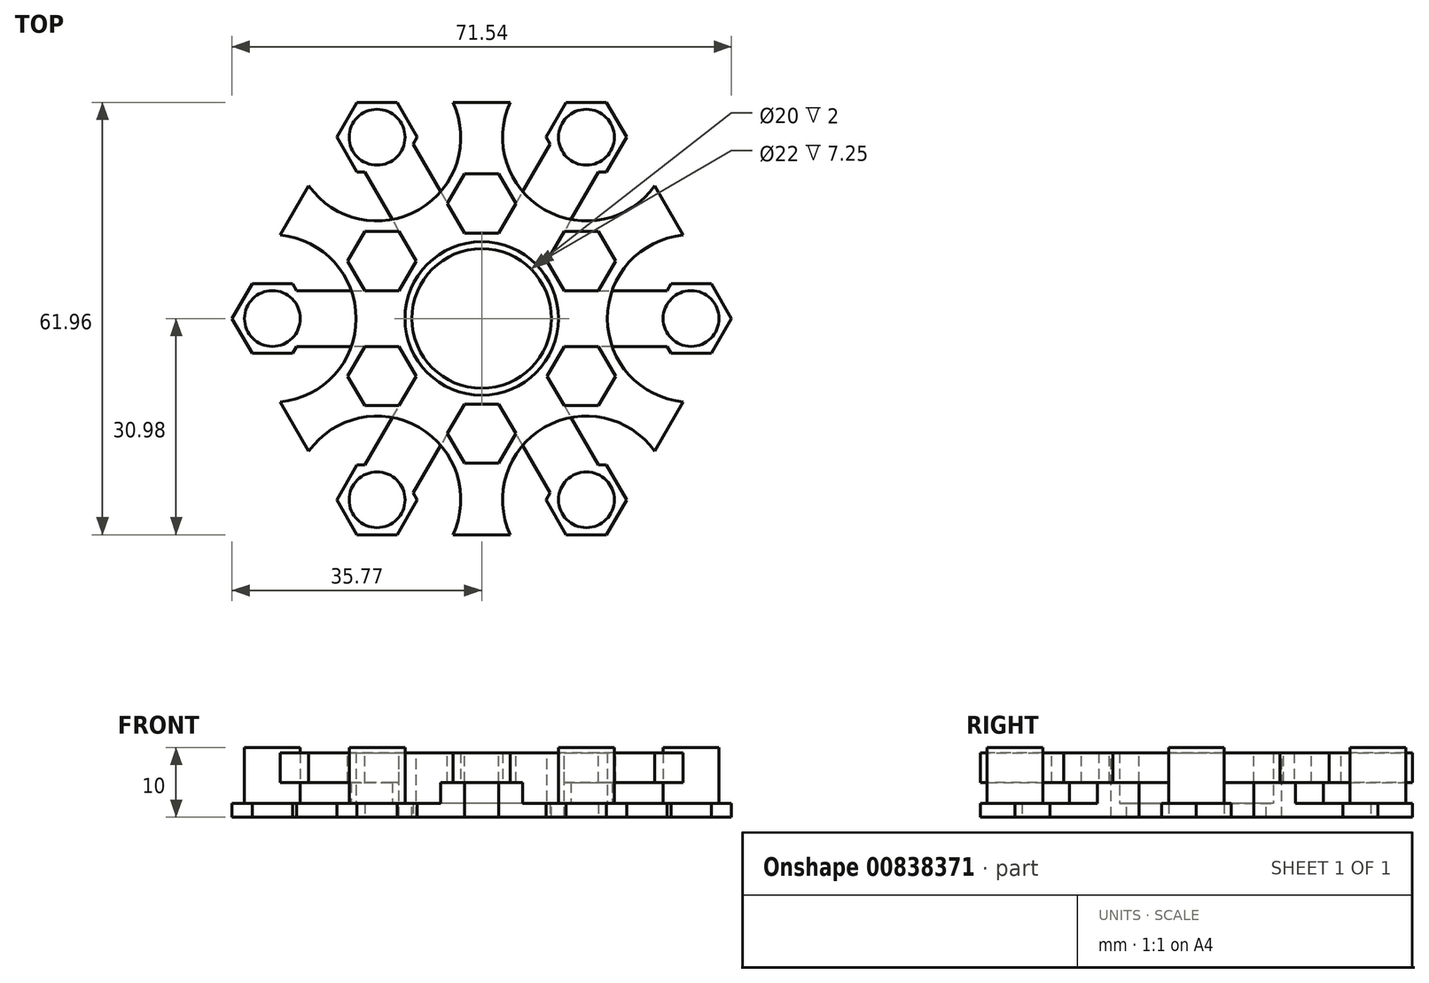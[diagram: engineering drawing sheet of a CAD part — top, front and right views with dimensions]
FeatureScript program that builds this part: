
annotation { "Feature Type Name" : "Feature", "Feature Type Description" : "" }
export const myFeature = defineFeature(function(context is Context, id is Id, definition is map)
    precondition{}
    {
        {
            var Q0;
            Q0=qCreatedBy(makeId("Top.planeOp"),FACE);
            var sketch = newSketch(context, id + "F0", { "sketchPlane" : qUnion([Q0])});
            skCircle(sketch, "E0", {"center": v(0, 0) * mm, "radius": 11 * mm});
            skCircle(sketch, "E1.cCircle", {"center": v(0, 0) * mm, "radius": 25.98 * mm, "construction": true});
            skLineSegment(sketch, "E1.0", {"start": v(-15, 25.98) * mm, "end": v(15, 25.98) * mm});
            skLineSegment(sketch, "E1.1", {"start": v(15, 25.98) * mm, "end": v(30, 0) * mm});
            skLineSegment(sketch, "E1.2", {"start": v(30, 0) * mm, "end": v(15, -25.98) * mm});
            skLineSegment(sketch, "E1.3", {"start": v(15, -25.98) * mm, "end": v(-15, -25.98) * mm});
            skLineSegment(sketch, "E1.4", {"start": v(-15, -25.98) * mm, "end": v(-30, 0) * mm});
            skLineSegment(sketch, "E1.5", {"start": v(-30, 0) * mm, "end": v(-15, 25.98) * mm});
            skPoint(sketch, "E1.0.midPoint", {"position": v(0, 25.98) * mm});
            skCircle(sketch, "E2", {"center": v(-15, 25.98) * mm, "radius": 11 * mm});
            skCircle(sketch, "E3", {"center": v(15, 25.98) * mm, "radius": 11 * mm});
            skCircle(sketch, "E4", {"center": v(30, 0) * mm, "radius": 11 * mm});
            skCircle(sketch, "E5", {"center": v(15, -25.98) * mm, "radius": 11 * mm});
            skCircle(sketch, "E6", {"center": v(-15, -25.98) * mm, "radius": 11 * mm});
            skCircle(sketch, "E7", {"center": v(-30, 0) * mm, "radius": 11 * mm});
            skCircle(sketch, "E8.cCircle", {"center": v(0, 0) * mm, "radius": 30.98 * mm, "construction": true});
            skLineSegment(sketch, "E8.0", {"start": v(-17.89, 30.98) * mm, "end": v(17.89, 30.98) * mm});
            skLineSegment(sketch, "E8.1", {"start": v(17.89, 30.98) * mm, "end": v(35.77, 0) * mm});
            skLineSegment(sketch, "E8.2", {"start": v(35.77, 0) * mm, "end": v(17.89, -30.98) * mm});
            skLineSegment(sketch, "E8.3", {"start": v(17.89, -30.98) * mm, "end": v(-17.89, -30.98) * mm});
            skLineSegment(sketch, "E8.4", {"start": v(-17.89, -30.98) * mm, "end": v(-35.77, 0) * mm});
            skLineSegment(sketch, "E8.5", {"start": v(-35.77, 0) * mm, "end": v(-17.89, 30.98) * mm});
            skPoint(sketch, "E8.0.midPoint", {"position": v(0, 30.98) * mm});
            skCircle(sketch, "E9", {"center": v(0, 0) * mm, "radius": 10 * mm});
            skCircle(sketch, "E10", {"center": v(-15, 25.98) * mm, "radius": 4 * mm});
            skCircle(sketch, "E11", {"center": v(-30, 0) * mm, "radius": 4 * mm});
            skCircle(sketch, "E12", {"center": v(-15, -25.98) * mm, "radius": 4 * mm});
            skCircle(sketch, "E13", {"center": v(15, -25.98) * mm, "radius": 4 * mm});
            skCircle(sketch, "E14", {"center": v(30, 0) * mm, "radius": 4 * mm});
            skCircle(sketch, "E15", {"center": v(15, 25.98) * mm, "radius": 4 * mm});
            skCircle(sketch, "E16", {"center": v(-30, 0) * mm, "radius": 12 * mm});
            skCircle(sketch, "E17", {"center": v(-15, 25.98) * mm, "radius": 12 * mm});
            skCircle(sketch, "E18", {"center": v(15, 25.98) * mm, "radius": 12 * mm});
            skCircle(sketch, "E19", {"center": v(30, 0) * mm, "radius": 12 * mm});
            skCircle(sketch, "E20", {"center": v(15, -25.98) * mm, "radius": 12 * mm});
            skCircle(sketch, "E21", {"center": v(-15, -25.98) * mm, "radius": 12 * mm});
            skSolve(sketch);
        }
        {
            var Q0;
            {var subQ0=sQuery(id+"F0.wireOp",EDGE,"E6");var subQ1=sQuery(id+"F0.wireOp",EDGE,"E1.4");var subQ2=makeQuery(id+"F0.imprint","INTERSECT",VERTEX,{"derivedFrom":[subQ1,subQ0]});Q0=makeQuery(id+"F0.imprint","IMPRINT",FACE,{"disambiguationData":[TD([[makeQuery(id+"F0.imprint","IMPRINT",EDGE,{"disambiguationData":[TD([[subQ2,-1.0]])],"derivedFrom":subQ1}),1.0]])]});}
            var Q1;
            {var subQ1=sQuery(id+"F0.wireOp",EDGE,"E6");var subQ3=sQuery(id+"F0.wireOp",EDGE,"E1.3");var subQ4=makeQuery(id+"F0.imprint","INTERSECT",VERTEX,{"derivedFrom":[subQ3,subQ1]});Q1=makeQuery(id+"F0.imprint","IMPRINT",FACE,{"disambiguationData":[TD([[makeQuery(id+"F0.imprint","IMPRINT",EDGE,{"disambiguationData":[TD([[subQ4,-1.0]])],"derivedFrom":subQ3}),1.0]])]});}
            var Q2;
            {var subQ0=sQuery(id+"F0.wireOp",EDGE,"E1.4");var subQ1=sQuery(id+"F0.wireOp",EDGE,"E1.3");var subQ2=makeQuery(id+"F0.imprint","INTERSECT",VERTEX,{"derivedFrom":[subQ1,subQ0]});Q2=makeQuery(id+"F0.imprint","IMPRINT",FACE,{"disambiguationData":[TD([[makeQuery(id+"F0.imprint","IMPRINT",EDGE,{"disambiguationData":[TD([[subQ2,1.0]])],"derivedFrom":subQ1}),1.0]])]});}
            var Q3;
            {var subQ0=sQuery(id+"F0.wireOp",EDGE,"E1.4");var subQ1=sQuery(id+"F0.wireOp",EDGE,"E1.3");var subQ2=makeQuery(id+"F0.imprint","INTERSECT",VERTEX,{"derivedFrom":[subQ1,subQ0]});Q3=makeQuery(id+"F0.imprint","IMPRINT",FACE,{"disambiguationData":[TD([[makeQuery(id+"F0.imprint","IMPRINT",EDGE,{"disambiguationData":[TD([[subQ2,1.0]])],"derivedFrom":subQ1}),-1.0]])]});}
            var Q4;
            {var subQ0=sQuery(id+"F0.wireOp",EDGE,"E6");var subQ1=sQuery(id+"F0.wireOp",EDGE,"E1.3");var subQ2=makeQuery(id+"F0.imprint","INTERSECT",VERTEX,{"derivedFrom":[subQ1,subQ0]});Q4=makeQuery(id+"F0.imprint","IMPRINT",FACE,{"disambiguationData":[TD([[makeQuery(id+"F0.imprint","IMPRINT",EDGE,{"disambiguationData":[TD([[subQ2,-1.0]])],"derivedFrom":subQ1}),-1.0]])]});}
            var Q5;
            {var subQ1=sQuery(id+"F0.wireOp",EDGE,"E7");var subQ3=sQuery(id+"F0.wireOp",EDGE,"E1.4");var subQ4=makeQuery(id+"F0.imprint","INTERSECT",VERTEX,{"derivedFrom":[subQ3,subQ1]});Q5=makeQuery(id+"F0.imprint","IMPRINT",FACE,{"disambiguationData":[TD([[makeQuery(id+"F0.imprint","IMPRINT",EDGE,{"disambiguationData":[TD([[subQ4,-1.0]])],"derivedFrom":subQ3}),1.0]])]});}
            var Q6;
            {var subQ0=sQuery(id+"F0.wireOp",EDGE,"E1.5");var subQ1=sQuery(id+"F0.wireOp",EDGE,"E1.4");var subQ2=makeQuery(id+"F0.imprint","INTERSECT",VERTEX,{"derivedFrom":[subQ1,subQ0]});Q6=makeQuery(id+"F0.imprint","IMPRINT",FACE,{"disambiguationData":[TD([[makeQuery(id+"F0.imprint","IMPRINT",EDGE,{"disambiguationData":[TD([[subQ2,1.0]])],"derivedFrom":subQ1}),-1.0]])]});}
            var Q7;
            {var subQ0=sQuery(id+"F0.wireOp",EDGE,"E1.5");var subQ1=sQuery(id+"F0.wireOp",EDGE,"E1.4");var subQ2=makeQuery(id+"F0.imprint","INTERSECT",VERTEX,{"derivedFrom":[subQ1,subQ0]});Q7=makeQuery(id+"F0.imprint","IMPRINT",FACE,{"disambiguationData":[TD([[makeQuery(id+"F0.imprint","IMPRINT",EDGE,{"disambiguationData":[TD([[subQ2,1.0]])],"derivedFrom":subQ1}),1.0]])]});}
            var Q8;
            {var subQ0=sQuery(id+"F0.wireOp",EDGE,"E7");var subQ1=sQuery(id+"F0.wireOp",EDGE,"E1.4");var subQ2=makeQuery(id+"F0.imprint","INTERSECT",VERTEX,{"derivedFrom":[subQ1,subQ0]});Q8=makeQuery(id+"F0.imprint","IMPRINT",FACE,{"disambiguationData":[TD([[makeQuery(id+"F0.imprint","IMPRINT",EDGE,{"disambiguationData":[TD([[subQ2,-1.0]])],"derivedFrom":subQ1}),-1.0]])]});}
            var Q9;
            Q9=makeQuery(id+"F0.imprint","IMPRINT",FACE,{"disambiguationData":[TD([[makeQuery(id+"F0.imprint","IMPRINT",EDGE,{"derivedFrom":sQuery(id+"F0.wireOp",EDGE,"E0")}),-1.0]])]});
            var Q10;
            Q10=makeQuery(id+"F0.imprint","IMPRINT",FACE,{"disambiguationData":[TD([[makeQuery(id+"F0.imprint","IMPRINT",EDGE,{"derivedFrom":sQuery(id+"F0.wireOp",EDGE,"E0")}),1.0]])]});
            var Q11;
            {var subQ0=sQuery(id+"F0.wireOp",EDGE,"E5");var subQ1=sQuery(id+"F0.wireOp",EDGE,"E1.3");var subQ2=makeQuery(id+"F0.imprint","INTERSECT",VERTEX,{"derivedFrom":[subQ1,subQ0]});Q11=makeQuery(id+"F0.imprint","IMPRINT",FACE,{"disambiguationData":[TD([[makeQuery(id+"F0.imprint","IMPRINT",EDGE,{"disambiguationData":[TD([[subQ2,-1.0]])],"derivedFrom":subQ1}),1.0]])]});}
            var Q12;
            {var subQ1=sQuery(id+"F0.wireOp",EDGE,"E5");var subQ7=sQuery(id+"F0.wireOp",EDGE,"E1.2");var subQ8=makeQuery(id+"F0.imprint","INTERSECT",VERTEX,{"derivedFrom":[subQ7,subQ1]});Q12=makeQuery(id+"F0.imprint","IMPRINT",FACE,{"disambiguationData":[TD([[makeQuery(id+"F0.imprint","IMPRINT",EDGE,{"disambiguationData":[TD([[subQ8,-1.0]])],"derivedFrom":subQ7}),1.0]])]});}
            var Q13;
            {var subQ0=sQuery(id+"F0.wireOp",EDGE,"E5");var subQ1=sQuery(id+"F0.wireOp",EDGE,"E1.2");var subQ2=makeQuery(id+"F0.imprint","INTERSECT",VERTEX,{"derivedFrom":[subQ1,subQ0]});Q13=makeQuery(id+"F0.imprint","IMPRINT",FACE,{"disambiguationData":[TD([[makeQuery(id+"F0.imprint","IMPRINT",EDGE,{"disambiguationData":[TD([[subQ2,-1.0]])],"derivedFrom":subQ1}),-1.0]])]});}
            var Q14;
            {var subQ0=sQuery(id+"F0.wireOp",EDGE,"E1.3");var subQ1=sQuery(id+"F0.wireOp",EDGE,"E1.2");var subQ2=makeQuery(id+"F0.imprint","INTERSECT",VERTEX,{"derivedFrom":[subQ1,subQ0]});Q14=makeQuery(id+"F0.imprint","IMPRINT",FACE,{"disambiguationData":[TD([[makeQuery(id+"F0.imprint","IMPRINT",EDGE,{"disambiguationData":[TD([[subQ2,1.0]])],"derivedFrom":subQ1}),1.0]])]});}
            var Q15;
            {var subQ0=sQuery(id+"F0.wireOp",EDGE,"E1.3");var subQ1=sQuery(id+"F0.wireOp",EDGE,"E1.2");var subQ2=makeQuery(id+"F0.imprint","INTERSECT",VERTEX,{"derivedFrom":[subQ1,subQ0]});Q15=makeQuery(id+"F0.imprint","IMPRINT",FACE,{"disambiguationData":[TD([[makeQuery(id+"F0.imprint","IMPRINT",EDGE,{"disambiguationData":[TD([[subQ2,1.0]])],"derivedFrom":subQ1}),-1.0]])]});}
            var Q16;
            {var subQ0=sQuery(id+"F0.wireOp",EDGE,"E4");var subQ1=sQuery(id+"F0.wireOp",EDGE,"E1.1");var subQ2=makeQuery(id+"F0.imprint","INTERSECT",VERTEX,{"derivedFrom":[subQ1,subQ0]});Q16=makeQuery(id+"F0.imprint","IMPRINT",FACE,{"disambiguationData":[TD([[makeQuery(id+"F0.imprint","IMPRINT",EDGE,{"disambiguationData":[TD([[subQ2,-1.0]])],"derivedFrom":subQ1}),-1.0]])]});}
            var Q17;
            {var subQ1=sQuery(id+"F0.wireOp",EDGE,"E4");var subQ9=sQuery(id+"F0.wireOp",EDGE,"E1.1");var subQ10=makeQuery(id+"F0.imprint","INTERSECT",VERTEX,{"derivedFrom":[subQ9,subQ1]});Q17=makeQuery(id+"F0.imprint","IMPRINT",FACE,{"disambiguationData":[TD([[makeQuery(id+"F0.imprint","IMPRINT",EDGE,{"disambiguationData":[TD([[subQ10,-1.0]])],"derivedFrom":subQ9}),1.0]])]});}
            var Q18;
            {var subQ0=sQuery(id+"F0.wireOp",EDGE,"E1.2");var subQ1=sQuery(id+"F0.wireOp",EDGE,"E1.1");var subQ2=makeQuery(id+"F0.imprint","INTERSECT",VERTEX,{"derivedFrom":[subQ1,subQ0]});Q18=makeQuery(id+"F0.imprint","IMPRINT",FACE,{"disambiguationData":[TD([[makeQuery(id+"F0.imprint","IMPRINT",EDGE,{"disambiguationData":[TD([[subQ2,1.0]])],"derivedFrom":subQ1}),1.0]])]});}
            var Q19;
            {var subQ0=sQuery(id+"F0.wireOp",EDGE,"E1.2");var subQ1=sQuery(id+"F0.wireOp",EDGE,"E1.1");var subQ2=makeQuery(id+"F0.imprint","INTERSECT",VERTEX,{"derivedFrom":[subQ1,subQ0]});Q19=makeQuery(id+"F0.imprint","IMPRINT",FACE,{"disambiguationData":[TD([[makeQuery(id+"F0.imprint","IMPRINT",EDGE,{"disambiguationData":[TD([[subQ2,1.0]])],"derivedFrom":subQ1}),-1.0]])]});}
            var Q20;
            {var subQ1=sQuery(id+"F0.wireOp",EDGE,"E3");var subQ3=sQuery(id+"F0.wireOp",EDGE,"E1.0");var subQ4=makeQuery(id+"F0.imprint","INTERSECT",VERTEX,{"derivedFrom":[subQ3,subQ1]});Q20=makeQuery(id+"F0.imprint","IMPRINT",FACE,{"disambiguationData":[TD([[makeQuery(id+"F0.imprint","IMPRINT",EDGE,{"disambiguationData":[TD([[subQ4,-1.0]])],"derivedFrom":subQ3}),1.0]])]});}
            var Q21;
            {var subQ0=sQuery(id+"F0.wireOp",EDGE,"E3");var subQ1=sQuery(id+"F0.wireOp",EDGE,"E1.0");var subQ2=makeQuery(id+"F0.imprint","INTERSECT",VERTEX,{"derivedFrom":[subQ1,subQ0]});Q21=makeQuery(id+"F0.imprint","IMPRINT",FACE,{"disambiguationData":[TD([[makeQuery(id+"F0.imprint","IMPRINT",EDGE,{"disambiguationData":[TD([[subQ2,-1.0]])],"derivedFrom":subQ1}),-1.0]])]});}
            var Q22;
            {var subQ0=sQuery(id+"F0.wireOp",EDGE,"E1.1");var subQ1=sQuery(id+"F0.wireOp",EDGE,"E1.0");var subQ2=makeQuery(id+"F0.imprint","INTERSECT",VERTEX,{"derivedFrom":[subQ1,subQ0]});Q22=makeQuery(id+"F0.imprint","IMPRINT",FACE,{"disambiguationData":[TD([[makeQuery(id+"F0.imprint","IMPRINT",EDGE,{"disambiguationData":[TD([[subQ2,1.0]])],"derivedFrom":subQ1}),-1.0]])]});}
            var Q23;
            {var subQ0=sQuery(id+"F0.wireOp",EDGE,"E1.1");var subQ1=sQuery(id+"F0.wireOp",EDGE,"E1.0");var subQ2=makeQuery(id+"F0.imprint","INTERSECT",VERTEX,{"derivedFrom":[subQ1,subQ0]});Q23=makeQuery(id+"F0.imprint","IMPRINT",FACE,{"disambiguationData":[TD([[makeQuery(id+"F0.imprint","IMPRINT",EDGE,{"disambiguationData":[TD([[subQ2,1.0]])],"derivedFrom":subQ1}),1.0]])]});}
            var Q24;
            {var subQ0=sQuery(id+"F0.wireOp",EDGE,"E10");var subQ1=sQuery(id+"F0.wireOp",EDGE,"E1.0");var subQ2=makeQuery(id+"F0.imprint","INTERSECT",VERTEX,{"derivedFrom":[subQ1,subQ0]});Q24=makeQuery(id+"F0.imprint","IMPRINT",FACE,{"disambiguationData":[TD([[makeQuery(id+"F0.imprint","IMPRINT",EDGE,{"disambiguationData":[TD([[subQ2,-1.0]])],"derivedFrom":subQ1}),-1.0]])]});}
            var Q25;
            {var subQ0=sQuery(id+"F0.wireOp",EDGE,"E7");var subQ1=sQuery(id+"F0.wireOp",EDGE,"E1.5");var subQ2=makeQuery(id+"F0.imprint","INTERSECT",VERTEX,{"derivedFrom":[subQ1,subQ0]});Q25=makeQuery(id+"F0.imprint","IMPRINT",FACE,{"disambiguationData":[TD([[makeQuery(id+"F0.imprint","IMPRINT",EDGE,{"disambiguationData":[TD([[subQ2,-1.0]])],"derivedFrom":subQ1}),1.0]])]});}
            var Q26;
            {var subQ8=sQuery(id+"F0.wireOp",EDGE,"E1.0");var subQ10=sQuery(id+"F0.wireOp",EDGE,"E10");var subQ12=makeQuery(id+"F0.imprint","INTERSECT",VERTEX,{"derivedFrom":[subQ8,subQ10]});Q26=makeQuery(id+"F0.imprint","IMPRINT",FACE,{"disambiguationData":[TD([[makeQuery(id+"F0.imprint","IMPRINT",EDGE,{"disambiguationData":[TD([[subQ12,-1.0]])],"derivedFrom":subQ8}),1.0]])]});}
            var Q27;
            {var subQ0=sQuery(id+"F0.wireOp",EDGE,"E1.5");var subQ1=sQuery(id+"F0.wireOp",EDGE,"E1.0");var subQ2=makeQuery(id+"F0.imprint","INTERSECT",VERTEX,{"derivedFrom":[subQ1,subQ0]});Q27=makeQuery(id+"F0.imprint","IMPRINT",FACE,{"disambiguationData":[TD([[makeQuery(id+"F0.imprint","IMPRINT",EDGE,{"disambiguationData":[TD([[subQ2,-1.0]])],"derivedFrom":subQ1}),-1.0]])]});}
            var Q28;
            {var subQ0=sQuery(id+"F0.wireOp",EDGE,"E1.5");var subQ1=sQuery(id+"F0.wireOp",EDGE,"E1.0");var subQ2=makeQuery(id+"F0.imprint","INTERSECT",VERTEX,{"derivedFrom":[subQ1,subQ0]});Q28=makeQuery(id+"F0.imprint","IMPRINT",FACE,{"disambiguationData":[TD([[makeQuery(id+"F0.imprint","IMPRINT",EDGE,{"disambiguationData":[TD([[subQ2,-1.0]])],"derivedFrom":subQ1}),1.0]])]});}
            var Q29;
            {var subQ0=sQuery(id+"F0.wireOp",EDGE,"E2");var subQ1=sQuery(id+"F0.wireOp",EDGE,"E1.0");var subQ2=makeQuery(id+"F0.imprint","INTERSECT",VERTEX,{"derivedFrom":[subQ1,subQ0]});Q29=makeQuery(id+"F0.imprint","IMPRINT",FACE,{"disambiguationData":[TD([[makeQuery(id+"F0.imprint","IMPRINT",EDGE,{"disambiguationData":[TD([[subQ2,-1.0]])],"derivedFrom":subQ1}),1.0]])]});}
            var Q30;
            {var subQ0=sQuery(id+"F0.wireOp",EDGE,"E3");var subQ1=sQuery(id+"F0.wireOp",EDGE,"E1.1");var subQ2=makeQuery(id+"F0.imprint","INTERSECT",VERTEX,{"derivedFrom":[subQ1,subQ0]});Q30=makeQuery(id+"F0.imprint","IMPRINT",FACE,{"disambiguationData":[TD([[makeQuery(id+"F0.imprint","IMPRINT",EDGE,{"disambiguationData":[TD([[subQ2,-1.0]])],"derivedFrom":subQ1}),1.0]])]});}
            var Q31;
            {var subQ0=sQuery(id+"F0.wireOp",EDGE,"E4");var subQ1=sQuery(id+"F0.wireOp",EDGE,"E1.2");var subQ2=makeQuery(id+"F0.imprint","INTERSECT",VERTEX,{"derivedFrom":[subQ1,subQ0]});Q31=makeQuery(id+"F0.imprint","IMPRINT",FACE,{"disambiguationData":[TD([[makeQuery(id+"F0.imprint","IMPRINT",EDGE,{"disambiguationData":[TD([[subQ2,-1.0]])],"derivedFrom":subQ1}),1.0]])]});}
            var Q32;
            {var subQ0=sQuery(id+"F0.wireOp",EDGE,"E16");var subQ1=sQuery(id+"F0.wireOp",EDGE,"E1.4");var subQ2=makeQuery(id+"F0.imprint","INTERSECT",VERTEX,{"derivedFrom":[subQ1,subQ0]});Q32=makeQuery(id+"F0.imprint","IMPRINT",FACE,{"disambiguationData":[TD([[makeQuery(id+"F0.imprint","IMPRINT",EDGE,{"disambiguationData":[TD([[subQ2,-1.0]])],"derivedFrom":subQ1}),-1.0]])]});}
            var Q33;
            {var subQ0=sQuery(id+"F0.wireOp",EDGE,"E2");var subQ1=sQuery(id+"F0.wireOp",EDGE,"E1.0");var subQ2=makeQuery(id+"F0.imprint","INTERSECT",VERTEX,{"derivedFrom":[subQ1,subQ0]});Q33=makeQuery(id+"F0.imprint","IMPRINT",FACE,{"disambiguationData":[TD([[makeQuery(id+"F0.imprint","IMPRINT",EDGE,{"disambiguationData":[TD([[subQ2,-1.0]])],"derivedFrom":subQ1}),-1.0]])]});}
            var Q34;
            {var subQ0=sQuery(id+"F0.wireOp",EDGE,"E21");var subQ1=sQuery(id+"F0.wireOp",EDGE,"E1.3");var subQ2=makeQuery(id+"F0.imprint","INTERSECT",VERTEX,{"derivedFrom":[subQ1,subQ0]});Q34=makeQuery(id+"F0.imprint","IMPRINT",FACE,{"disambiguationData":[TD([[makeQuery(id+"F0.imprint","IMPRINT",EDGE,{"disambiguationData":[TD([[subQ2,-1.0]])],"derivedFrom":subQ1}),-1.0]])]});}
            var Q35;
            {var subQ0=sQuery(id+"F0.wireOp",EDGE,"E20");var subQ1=sQuery(id+"F0.wireOp",EDGE,"E1.2");var subQ2=makeQuery(id+"F0.imprint","INTERSECT",VERTEX,{"derivedFrom":[subQ1,subQ0]});Q35=makeQuery(id+"F0.imprint","IMPRINT",FACE,{"disambiguationData":[TD([[makeQuery(id+"F0.imprint","IMPRINT",EDGE,{"disambiguationData":[TD([[subQ2,-1.0]])],"derivedFrom":subQ1}),-1.0]])]});}
            var Q36;
            {var subQ0=sQuery(id+"F0.wireOp",EDGE,"E19");var subQ1=sQuery(id+"F0.wireOp",EDGE,"E1.1");var subQ2=makeQuery(id+"F0.imprint","INTERSECT",VERTEX,{"derivedFrom":[subQ1,subQ0]});Q36=makeQuery(id+"F0.imprint","IMPRINT",FACE,{"disambiguationData":[TD([[makeQuery(id+"F0.imprint","IMPRINT",EDGE,{"disambiguationData":[TD([[subQ2,-1.0]])],"derivedFrom":subQ1}),-1.0]])]});}
            var Q37;
            {var subQ0=sQuery(id+"F0.wireOp",EDGE,"E18");var subQ1=sQuery(id+"F0.wireOp",EDGE,"E1.0");var subQ2=makeQuery(id+"F0.imprint","INTERSECT",VERTEX,{"derivedFrom":[subQ1,subQ0]});Q37=makeQuery(id+"F0.imprint","IMPRINT",FACE,{"disambiguationData":[TD([[makeQuery(id+"F0.imprint","IMPRINT",EDGE,{"disambiguationData":[TD([[subQ2,-1.0]])],"derivedFrom":subQ1}),-1.0]])]});}
            var Q38;
            {var subQ0=sQuery(id+"F0.wireOp",EDGE,"E17");var subQ1=sQuery(id+"F0.wireOp",EDGE,"E1.0");var subQ2=makeQuery(id+"F0.imprint","INTERSECT",VERTEX,{"derivedFrom":[subQ1,subQ0]});Q38=makeQuery(id+"F0.imprint","IMPRINT",FACE,{"disambiguationData":[TD([[makeQuery(id+"F0.imprint","IMPRINT",EDGE,{"disambiguationData":[TD([[subQ2,-1.0]])],"derivedFrom":subQ1}),1.0]])]});}
            var Q39;
            {var subQ0=sQuery(id+"F0.wireOp",EDGE,"E16");var subQ1=sQuery(id+"F0.wireOp",EDGE,"E1.5");var subQ2=makeQuery(id+"F0.imprint","INTERSECT",VERTEX,{"derivedFrom":[subQ1,subQ0]});Q39=makeQuery(id+"F0.imprint","IMPRINT",FACE,{"disambiguationData":[TD([[makeQuery(id+"F0.imprint","IMPRINT",EDGE,{"disambiguationData":[TD([[subQ2,-1.0]])],"derivedFrom":subQ1}),1.0]])]});}
            var Q40;
            {var subQ0=sQuery(id+"F0.wireOp",EDGE,"E21");var subQ1=sQuery(id+"F0.wireOp",EDGE,"E1.4");var subQ2=makeQuery(id+"F0.imprint","INTERSECT",VERTEX,{"derivedFrom":[subQ1,subQ0]});Q40=makeQuery(id+"F0.imprint","IMPRINT",FACE,{"disambiguationData":[TD([[makeQuery(id+"F0.imprint","IMPRINT",EDGE,{"disambiguationData":[TD([[subQ2,-1.0]])],"derivedFrom":subQ1}),1.0]])]});}
            var Q41;
            {var subQ0=sQuery(id+"F0.wireOp",EDGE,"E20");var subQ1=sQuery(id+"F0.wireOp",EDGE,"E1.3");var subQ2=makeQuery(id+"F0.imprint","INTERSECT",VERTEX,{"derivedFrom":[subQ1,subQ0]});Q41=makeQuery(id+"F0.imprint","IMPRINT",FACE,{"disambiguationData":[TD([[makeQuery(id+"F0.imprint","IMPRINT",EDGE,{"disambiguationData":[TD([[subQ2,-1.0]])],"derivedFrom":subQ1}),1.0]])]});}
            var Q42;
            {var subQ0=sQuery(id+"F0.wireOp",EDGE,"E19");var subQ1=sQuery(id+"F0.wireOp",EDGE,"E1.2");var subQ2=makeQuery(id+"F0.imprint","INTERSECT",VERTEX,{"derivedFrom":[subQ1,subQ0]});Q42=makeQuery(id+"F0.imprint","IMPRINT",FACE,{"disambiguationData":[TD([[makeQuery(id+"F0.imprint","IMPRINT",EDGE,{"disambiguationData":[TD([[subQ2,-1.0]])],"derivedFrom":subQ1}),1.0]])]});}
            var Q43;
            {var subQ0=sQuery(id+"F0.wireOp",EDGE,"E18");var subQ1=sQuery(id+"F0.wireOp",EDGE,"E1.1");var subQ2=makeQuery(id+"F0.imprint","INTERSECT",VERTEX,{"derivedFrom":[subQ1,subQ0]});Q43=makeQuery(id+"F0.imprint","IMPRINT",FACE,{"disambiguationData":[TD([[makeQuery(id+"F0.imprint","IMPRINT",EDGE,{"disambiguationData":[TD([[subQ2,-1.0]])],"derivedFrom":subQ1}),1.0]])]});}
            var Q44;
            {var subQ0=sQuery(id+"F0.wireOp",EDGE,"E18");var subQ1=sQuery(id+"F0.wireOp",EDGE,"E1.0");var subQ2=makeQuery(id+"F0.imprint","INTERSECT",VERTEX,{"derivedFrom":[subQ1,subQ0]});Q44=makeQuery(id+"F0.imprint","IMPRINT",FACE,{"disambiguationData":[TD([[makeQuery(id+"F0.imprint","IMPRINT",EDGE,{"disambiguationData":[TD([[subQ2,-1.0]])],"derivedFrom":subQ1}),1.0]])]});}
            var Q45;
            {var subQ0=sQuery(id+"F0.wireOp",EDGE,"E17");var subQ1=sQuery(id+"F0.wireOp",EDGE,"E1.5");var subQ2=makeQuery(id+"F0.imprint","INTERSECT",VERTEX,{"derivedFrom":[subQ1,subQ0]});Q45=makeQuery(id+"F0.imprint","IMPRINT",FACE,{"disambiguationData":[TD([[makeQuery(id+"F0.imprint","IMPRINT",EDGE,{"disambiguationData":[TD([[subQ2,-1.0]])],"derivedFrom":subQ1}),1.0]])]});}
            var Q46;
            {var subQ0=sQuery(id+"F0.wireOp",EDGE,"E16");var subQ1=sQuery(id+"F0.wireOp",EDGE,"E1.4");var subQ2=makeQuery(id+"F0.imprint","INTERSECT",VERTEX,{"derivedFrom":[subQ1,subQ0]});Q46=makeQuery(id+"F0.imprint","IMPRINT",FACE,{"disambiguationData":[TD([[makeQuery(id+"F0.imprint","IMPRINT",EDGE,{"disambiguationData":[TD([[subQ2,-1.0]])],"derivedFrom":subQ1}),1.0]])]});}
            var Q47;
            {var subQ0=sQuery(id+"F0.wireOp",EDGE,"E21");var subQ1=sQuery(id+"F0.wireOp",EDGE,"E1.3");var subQ2=makeQuery(id+"F0.imprint","INTERSECT",VERTEX,{"derivedFrom":[subQ1,subQ0]});Q47=makeQuery(id+"F0.imprint","IMPRINT",FACE,{"disambiguationData":[TD([[makeQuery(id+"F0.imprint","IMPRINT",EDGE,{"disambiguationData":[TD([[subQ2,-1.0]])],"derivedFrom":subQ1}),1.0]])]});}
            var Q48;
            {var subQ0=sQuery(id+"F0.wireOp",EDGE,"E20");var subQ1=sQuery(id+"F0.wireOp",EDGE,"E1.2");var subQ2=makeQuery(id+"F0.imprint","INTERSECT",VERTEX,{"derivedFrom":[subQ1,subQ0]});Q48=makeQuery(id+"F0.imprint","IMPRINT",FACE,{"disambiguationData":[TD([[makeQuery(id+"F0.imprint","IMPRINT",EDGE,{"disambiguationData":[TD([[subQ2,-1.0]])],"derivedFrom":subQ1}),1.0]])]});}
            var Q49;
            {var subQ0=sQuery(id+"F0.wireOp",EDGE,"E19");var subQ1=sQuery(id+"F0.wireOp",EDGE,"E1.1");var subQ2=makeQuery(id+"F0.imprint","INTERSECT",VERTEX,{"derivedFrom":[subQ1,subQ0]});Q49=makeQuery(id+"F0.imprint","IMPRINT",FACE,{"disambiguationData":[TD([[makeQuery(id+"F0.imprint","IMPRINT",EDGE,{"disambiguationData":[TD([[subQ2,-1.0]])],"derivedFrom":subQ1}),1.0]])]});}
            extrude(context, id + "F1", {"entities" : qUnion([Q0, Q1, Q2, Q3, Q4, Q5, Q6, Q7, Q8, Q9, Q10, Q11, Q12, Q13, Q14, Q15, Q16, Q17, Q18, Q19, Q20, Q21, Q22, Q23, Q24, Q25, Q26, Q27, Q28, Q29, Q30, Q31, Q32, Q33, Q34, Q35, Q36, Q37, Q38, Q39, Q40, Q41, Q42, Q43, Q44, Q45, Q46, Q47, Q48, Q49]), "oppositeDirection" : true, "depth" : 2 * mm, "offsetDistance" : 25 * mm});
        }
        {
            var Q0;
            Q0=makeQuery(id+"F0.imprint","IMPRINT",FACE,{"disambiguationData":[TD([[makeQuery(id+"F0.imprint","IMPRINT",EDGE,{"derivedFrom":sQuery(id+"F0.wireOp",EDGE,"E0")}),-1.0]])]});
            var Q1;
            {var subQ0=sQuery(id+"F0.wireOp",EDGE,"E16");var subQ1=sQuery(id+"F0.wireOp",EDGE,"E1.5");var subQ2=makeQuery(id+"F0.imprint","INTERSECT",VERTEX,{"derivedFrom":[subQ1,subQ0]});Q1=makeQuery(id+"F0.imprint","IMPRINT",FACE,{"disambiguationData":[TD([[makeQuery(id+"F0.imprint","IMPRINT",EDGE,{"disambiguationData":[TD([[subQ2,-1.0]])],"derivedFrom":subQ1}),1.0]])]});}
            var Q2;
            {var subQ0=sQuery(id+"F0.wireOp",EDGE,"E17");var subQ1=sQuery(id+"F0.wireOp",EDGE,"E1.0");var subQ2=makeQuery(id+"F0.imprint","INTERSECT",VERTEX,{"derivedFrom":[subQ1,subQ0]});Q2=makeQuery(id+"F0.imprint","IMPRINT",FACE,{"disambiguationData":[TD([[makeQuery(id+"F0.imprint","IMPRINT",EDGE,{"disambiguationData":[TD([[subQ2,-1.0]])],"derivedFrom":subQ1}),1.0]])]});}
            var Q3;
            {var subQ0=sQuery(id+"F0.wireOp",EDGE,"E18");var subQ1=sQuery(id+"F0.wireOp",EDGE,"E1.1");var subQ2=makeQuery(id+"F0.imprint","INTERSECT",VERTEX,{"derivedFrom":[subQ1,subQ0]});Q3=makeQuery(id+"F0.imprint","IMPRINT",FACE,{"disambiguationData":[TD([[makeQuery(id+"F0.imprint","IMPRINT",EDGE,{"disambiguationData":[TD([[subQ2,-1.0]])],"derivedFrom":subQ1}),1.0]])]});}
            var Q4;
            {var subQ0=sQuery(id+"F0.wireOp",EDGE,"E19");var subQ1=sQuery(id+"F0.wireOp",EDGE,"E1.2");var subQ2=makeQuery(id+"F0.imprint","INTERSECT",VERTEX,{"derivedFrom":[subQ1,subQ0]});Q4=makeQuery(id+"F0.imprint","IMPRINT",FACE,{"disambiguationData":[TD([[makeQuery(id+"F0.imprint","IMPRINT",EDGE,{"disambiguationData":[TD([[subQ2,-1.0]])],"derivedFrom":subQ1}),1.0]])]});}
            var Q5;
            {var subQ0=sQuery(id+"F0.wireOp",EDGE,"E20");var subQ1=sQuery(id+"F0.wireOp",EDGE,"E1.3");var subQ2=makeQuery(id+"F0.imprint","INTERSECT",VERTEX,{"derivedFrom":[subQ1,subQ0]});Q5=makeQuery(id+"F0.imprint","IMPRINT",FACE,{"disambiguationData":[TD([[makeQuery(id+"F0.imprint","IMPRINT",EDGE,{"disambiguationData":[TD([[subQ2,-1.0]])],"derivedFrom":subQ1}),1.0]])]});}
            var Q6;
            {var subQ0=sQuery(id+"F0.wireOp",EDGE,"E21");var subQ1=sQuery(id+"F0.wireOp",EDGE,"E1.4");var subQ2=makeQuery(id+"F0.imprint","INTERSECT",VERTEX,{"derivedFrom":[subQ1,subQ0]});Q6=makeQuery(id+"F0.imprint","IMPRINT",FACE,{"disambiguationData":[TD([[makeQuery(id+"F0.imprint","IMPRINT",EDGE,{"disambiguationData":[TD([[subQ2,-1.0]])],"derivedFrom":subQ1}),1.0]])]});}
            extrude(context, id + "F2", {"entities" : qUnion([Q0, Q1, Q2, Q3, Q4, Q5, Q6]), "operationType" : NewBodyOperationType.ADD, "depth" : 7.25 * mm, "offsetDistance" : 25 * mm});
        }
        {
            var Q0;
            Q0=makeQuery(id+"F2.opExtrude","CAP_FACE",FACE,{"disambiguationData":[OSD([sQuery(id+"F0.wireOp",EDGE,"E0"),sQuery(id+"F0.wireOp",EDGE,"E8.0"),sQuery(id+"F0.wireOp",EDGE,"E8.1"),sQuery(id+"F0.wireOp",EDGE,"E8.2"),sQuery(id+"F0.wireOp",EDGE,"E8.3"),sQuery(id+"F0.wireOp",EDGE,"E8.4"),sQuery(id+"F0.wireOp",EDGE,"E8.5"),sQuery(id+"F0.wireOp",EDGE,"E16"),sQuery(id+"F0.wireOp",EDGE,"E17"),sQuery(id+"F0.wireOp",EDGE,"E18"),sQuery(id+"F0.wireOp",EDGE,"E19"),sQuery(id+"F0.wireOp",EDGE,"E20"),sQuery(id+"F0.wireOp",EDGE,"E21")])],"isStart":false});
            var sketch = newSketch(context, id + "F3", { "sketchPlane" : qUnion([Q0])});
            skLineSegment(sketch, "E22", {"start": v(0, 0) * mm, "end": v(-26.83, 15.5) * mm, "construction": true});
            skLineSegment(sketch, "E23", {"start": v(0, 0) * mm, "end": v(0, 30.98) * mm, "construction": true});
            skLineSegment(sketch, "E24", {"start": v(26.83, -15.5) * mm, "end": v(0, 0) * mm, "construction": true});
            skLineSegment(sketch, "E25", {"start": v(0, -30.98) * mm, "end": v(0, 0) * mm, "construction": true});
            skLineSegment(sketch, "E26", {"start": v(-26.83, -15.5) * mm, "end": v(0, 0) * mm, "construction": true});
            skLineSegment(sketch, "E27", {"start": v(26.83, 15.5) * mm, "end": v(0, 0) * mm, "construction": true});
            skCircle(sketch, "E28", {"center": v(0, 0) * mm, "radius": 16.5 * mm, "construction": true});
            skCircle(sketch, "E29.cCircle", {"center": v(-14.29, 8.25) * mm, "radius": 4.25 * mm, "construction": true});
            skLineSegment(sketch, "E29.0", {"start": v(-9.38, 8.25) * mm, "end": v(-11.84, 4) * mm});
            skLineSegment(sketch, "E29.1", {"start": v(-11.84, 4) * mm, "end": v(-16.74, 4) * mm});
            skLineSegment(sketch, "E29.2", {"start": v(-16.74, 4) * mm, "end": v(-19.2, 8.25) * mm});
            skLineSegment(sketch, "E29.3", {"start": v(-19.2, 8.25) * mm, "end": v(-16.74, 12.5) * mm});
            skLineSegment(sketch, "E29.4", {"start": v(-16.74, 12.5) * mm, "end": v(-11.84, 12.5) * mm});
            skLineSegment(sketch, "E29.5", {"start": v(-11.84, 12.5) * mm, "end": v(-9.38, 8.25) * mm});
            skPoint(sketch, "E29.0.midPoint", {"position": v(-10.6, 6.13) * mm});
            skLineSegment(sketch, "E30.1.0", {"start": v(-19.2, -8.25) * mm, "end": v(-16.74, -4) * mm});
            skLineSegment(sketch, "E30.1.1", {"start": v(-16.74, -12.5) * mm, "end": v(-19.2, -8.25) * mm});
            skLineSegment(sketch, "E30.1.2", {"start": v(-11.84, -12.5) * mm, "end": v(-16.74, -12.5) * mm});
            skLineSegment(sketch, "E30.1.3", {"start": v(-9.38, -8.25) * mm, "end": v(-11.84, -12.5) * mm});
            skLineSegment(sketch, "E30.1.4", {"start": v(-11.84, -4) * mm, "end": v(-9.38, -8.25) * mm});
            skLineSegment(sketch, "E30.1.5", {"start": v(-16.74, -4) * mm, "end": v(-11.84, -4) * mm});
            skLineSegment(sketch, "E30.2.0", {"start": v(-2.45, -20.75) * mm, "end": v(-4.9, -16.5) * mm});
            skLineSegment(sketch, "E30.2.1", {"start": v(2.45, -20.75) * mm, "end": v(-2.45, -20.75) * mm});
            skLineSegment(sketch, "E30.2.2", {"start": v(4.9, -16.5) * mm, "end": v(2.45, -20.75) * mm});
            skLineSegment(sketch, "E30.2.3", {"start": v(2.45, -12.25) * mm, "end": v(4.9, -16.5) * mm});
            skLineSegment(sketch, "E30.2.4", {"start": v(-2.45, -12.25) * mm, "end": v(2.45, -12.25) * mm});
            skLineSegment(sketch, "E30.2.5", {"start": v(-4.9, -16.5) * mm, "end": v(-2.45, -12.25) * mm});
            skLineSegment(sketch, "E30.3.0", {"start": v(16.74, -12.5) * mm, "end": v(11.84, -12.5) * mm});
            skLineSegment(sketch, "E30.3.1", {"start": v(19.2, -8.25) * mm, "end": v(16.74, -12.5) * mm});
            skLineSegment(sketch, "E30.3.2", {"start": v(16.74, -4) * mm, "end": v(19.2, -8.25) * mm});
            skLineSegment(sketch, "E30.3.3", {"start": v(11.84, -4) * mm, "end": v(16.74, -4) * mm});
            skLineSegment(sketch, "E30.3.4", {"start": v(9.38, -8.25) * mm, "end": v(11.84, -4) * mm});
            skLineSegment(sketch, "E30.3.5", {"start": v(11.84, -12.5) * mm, "end": v(9.38, -8.25) * mm});
            skLineSegment(sketch, "E30.4.0", {"start": v(19.2, 8.25) * mm, "end": v(16.74, 4) * mm});
            skLineSegment(sketch, "E30.4.1", {"start": v(16.74, 12.5) * mm, "end": v(19.2, 8.25) * mm});
            skLineSegment(sketch, "E30.4.2", {"start": v(11.84, 12.5) * mm, "end": v(16.74, 12.5) * mm});
            skLineSegment(sketch, "E30.4.3", {"start": v(9.38, 8.25) * mm, "end": v(11.84, 12.5) * mm});
            skLineSegment(sketch, "E30.4.4", {"start": v(11.84, 4) * mm, "end": v(9.38, 8.25) * mm});
            skLineSegment(sketch, "E30.4.5", {"start": v(16.74, 4) * mm, "end": v(11.84, 4) * mm});
            skLineSegment(sketch, "E30.5.0", {"start": v(2.45, 20.75) * mm, "end": v(4.9, 16.5) * mm});
            skLineSegment(sketch, "E30.5.1", {"start": v(-2.45, 20.75) * mm, "end": v(2.45, 20.75) * mm});
            skLineSegment(sketch, "E30.5.2", {"start": v(-4.9, 16.5) * mm, "end": v(-2.45, 20.75) * mm});
            skLineSegment(sketch, "E30.5.3", {"start": v(-2.45, 12.25) * mm, "end": v(-4.9, 16.5) * mm});
            skLineSegment(sketch, "E30.5.4", {"start": v(2.45, 12.25) * mm, "end": v(-2.45, 12.25) * mm});
            skLineSegment(sketch, "E30.5.5", {"start": v(4.9, 16.5) * mm, "end": v(2.45, 12.25) * mm});
            skSolve(sketch);
        }
        {
            var Q0;
            Q0 = qSketchRegion(id + "F3", true);
            extrude(context, id + "F4", {"entities" : qUnion([Q0]), "operationType" : NewBodyOperationType.REMOVE, "oppositeDirection" : true, "depth" : 25 * mm, "offsetDistance" : 25 * mm});
        }
        {
            var Q0;
            {var subQ0=sQuery(id+"F0.wireOp",EDGE,"E1.5");var subQ1=sQuery(id+"F0.wireOp",EDGE,"E1.0");var subQ2=makeQuery(id+"F0.imprint","INTERSECT",VERTEX,{"derivedFrom":[subQ1,subQ0]});Q0=makeQuery(id+"F0.imprint","IMPRINT",FACE,{"disambiguationData":[TD([[makeQuery(id+"F0.imprint","IMPRINT",EDGE,{"disambiguationData":[TD([[subQ2,-1.0]])],"derivedFrom":subQ1}),-1.0]])]});}
            var Q1;
            {var subQ0=sQuery(id+"F0.wireOp",EDGE,"E1.5");var subQ1=sQuery(id+"F0.wireOp",EDGE,"E1.0");var subQ2=makeQuery(id+"F0.imprint","INTERSECT",VERTEX,{"derivedFrom":[subQ1,subQ0]});Q1=makeQuery(id+"F0.imprint","IMPRINT",FACE,{"disambiguationData":[TD([[makeQuery(id+"F0.imprint","IMPRINT",EDGE,{"disambiguationData":[TD([[subQ2,-1.0]])],"derivedFrom":subQ1}),1.0]])]});}
            var Q2;
            {var subQ0=sQuery(id+"F0.wireOp",EDGE,"E1.1");var subQ1=sQuery(id+"F0.wireOp",EDGE,"E1.0");var subQ2=makeQuery(id+"F0.imprint","INTERSECT",VERTEX,{"derivedFrom":[subQ1,subQ0]});Q2=makeQuery(id+"F0.imprint","IMPRINT",FACE,{"disambiguationData":[TD([[makeQuery(id+"F0.imprint","IMPRINT",EDGE,{"disambiguationData":[TD([[subQ2,1.0]])],"derivedFrom":subQ1}),-1.0]])]});}
            var Q3;
            {var subQ0=sQuery(id+"F0.wireOp",EDGE,"E1.1");var subQ1=sQuery(id+"F0.wireOp",EDGE,"E1.0");var subQ2=makeQuery(id+"F0.imprint","INTERSECT",VERTEX,{"derivedFrom":[subQ1,subQ0]});Q3=makeQuery(id+"F0.imprint","IMPRINT",FACE,{"disambiguationData":[TD([[makeQuery(id+"F0.imprint","IMPRINT",EDGE,{"disambiguationData":[TD([[subQ2,1.0]])],"derivedFrom":subQ1}),1.0]])]});}
            var Q4;
            {var subQ0=sQuery(id+"F0.wireOp",EDGE,"E1.2");var subQ1=sQuery(id+"F0.wireOp",EDGE,"E1.1");var subQ2=makeQuery(id+"F0.imprint","INTERSECT",VERTEX,{"derivedFrom":[subQ1,subQ0]});Q4=makeQuery(id+"F0.imprint","IMPRINT",FACE,{"disambiguationData":[TD([[makeQuery(id+"F0.imprint","IMPRINT",EDGE,{"disambiguationData":[TD([[subQ2,1.0]])],"derivedFrom":subQ1}),1.0]])]});}
            var Q5;
            {var subQ0=sQuery(id+"F0.wireOp",EDGE,"E1.2");var subQ1=sQuery(id+"F0.wireOp",EDGE,"E1.1");var subQ2=makeQuery(id+"F0.imprint","INTERSECT",VERTEX,{"derivedFrom":[subQ1,subQ0]});Q5=makeQuery(id+"F0.imprint","IMPRINT",FACE,{"disambiguationData":[TD([[makeQuery(id+"F0.imprint","IMPRINT",EDGE,{"disambiguationData":[TD([[subQ2,1.0]])],"derivedFrom":subQ1}),-1.0]])]});}
            var Q6;
            {var subQ0=sQuery(id+"F0.wireOp",EDGE,"E1.5");var subQ1=sQuery(id+"F0.wireOp",EDGE,"E1.4");var subQ2=makeQuery(id+"F0.imprint","INTERSECT",VERTEX,{"derivedFrom":[subQ1,subQ0]});Q6=makeQuery(id+"F0.imprint","IMPRINT",FACE,{"disambiguationData":[TD([[makeQuery(id+"F0.imprint","IMPRINT",EDGE,{"disambiguationData":[TD([[subQ2,1.0]])],"derivedFrom":subQ1}),-1.0]])]});}
            var Q7;
            {var subQ0=sQuery(id+"F0.wireOp",EDGE,"E1.5");var subQ1=sQuery(id+"F0.wireOp",EDGE,"E1.4");var subQ2=makeQuery(id+"F0.imprint","INTERSECT",VERTEX,{"derivedFrom":[subQ1,subQ0]});Q7=makeQuery(id+"F0.imprint","IMPRINT",FACE,{"disambiguationData":[TD([[makeQuery(id+"F0.imprint","IMPRINT",EDGE,{"disambiguationData":[TD([[subQ2,1.0]])],"derivedFrom":subQ1}),1.0]])]});}
            var Q8;
            {var subQ0=sQuery(id+"F0.wireOp",EDGE,"E1.4");var subQ1=sQuery(id+"F0.wireOp",EDGE,"E1.3");var subQ2=makeQuery(id+"F0.imprint","INTERSECT",VERTEX,{"derivedFrom":[subQ1,subQ0]});Q8=makeQuery(id+"F0.imprint","IMPRINT",FACE,{"disambiguationData":[TD([[makeQuery(id+"F0.imprint","IMPRINT",EDGE,{"disambiguationData":[TD([[subQ2,1.0]])],"derivedFrom":subQ1}),1.0]])]});}
            var Q9;
            {var subQ0=sQuery(id+"F0.wireOp",EDGE,"E1.4");var subQ1=sQuery(id+"F0.wireOp",EDGE,"E1.3");var subQ2=makeQuery(id+"F0.imprint","INTERSECT",VERTEX,{"derivedFrom":[subQ1,subQ0]});Q9=makeQuery(id+"F0.imprint","IMPRINT",FACE,{"disambiguationData":[TD([[makeQuery(id+"F0.imprint","IMPRINT",EDGE,{"disambiguationData":[TD([[subQ2,1.0]])],"derivedFrom":subQ1}),-1.0]])]});}
            var Q10;
            {var subQ0=sQuery(id+"F0.wireOp",EDGE,"E1.3");var subQ1=sQuery(id+"F0.wireOp",EDGE,"E1.2");var subQ2=makeQuery(id+"F0.imprint","INTERSECT",VERTEX,{"derivedFrom":[subQ1,subQ0]});Q10=makeQuery(id+"F0.imprint","IMPRINT",FACE,{"disambiguationData":[TD([[makeQuery(id+"F0.imprint","IMPRINT",EDGE,{"disambiguationData":[TD([[subQ2,1.0]])],"derivedFrom":subQ1}),-1.0]])]});}
            var Q11;
            {var subQ0=sQuery(id+"F0.wireOp",EDGE,"E1.3");var subQ1=sQuery(id+"F0.wireOp",EDGE,"E1.2");var subQ2=makeQuery(id+"F0.imprint","INTERSECT",VERTEX,{"derivedFrom":[subQ1,subQ0]});Q11=makeQuery(id+"F0.imprint","IMPRINT",FACE,{"disambiguationData":[TD([[makeQuery(id+"F0.imprint","IMPRINT",EDGE,{"disambiguationData":[TD([[subQ2,1.0]])],"derivedFrom":subQ1}),1.0]])]});}
            extrude(context, id + "F5", {"entities" : qUnion([Q0, Q1, Q2, Q3, Q4, Q5, Q6, Q7, Q8, Q9, Q10, Q11]), "operationType" : NewBodyOperationType.ADD, "depth" : 8 * mm, "offsetDistance" : 25 * mm});
        }
        {
            var Q0;
            Q0=makeQuery(id+"F1.opExtrude","CAP_FACE",FACE,{"disambiguationData":[OSD([sQuery(id+"F0.wireOp",EDGE,"E8.0"),sQuery(id+"F0.wireOp",EDGE,"E8.1"),sQuery(id+"F0.wireOp",EDGE,"E8.2"),sQuery(id+"F0.wireOp",EDGE,"E8.3"),sQuery(id+"F0.wireOp",EDGE,"E8.4"),sQuery(id+"F0.wireOp",EDGE,"E8.5"),sQuery(id+"F0.wireOp",EDGE,"E9")])],"isStart":false});
            var sketch = newSketch(context, id + "F6", { "sketchPlane" : qUnion([Q0])});
            skCircle(sketch, "E31.cCircle", {"center": v(-30, 0) * mm, "radius": 5 * mm, "construction": true});
            skLineSegment(sketch, "E31.0", {"start": v(-32.89, -5) * mm, "end": v(-35.77, 0) * mm});
            skLineSegment(sketch, "E31.1", {"start": v(-35.77, 0) * mm, "end": v(-32.89, 5) * mm});
            skLineSegment(sketch, "E31.2", {"start": v(-32.89, 5) * mm, "end": v(-27.11, 5) * mm});
            skLineSegment(sketch, "E31.3", {"start": v(-27.11, 5) * mm, "end": v(-24.23, 0) * mm});
            skLineSegment(sketch, "E31.4", {"start": v(-24.23, 0) * mm, "end": v(-27.11, -5) * mm});
            skLineSegment(sketch, "E31.5", {"start": v(-27.11, -5) * mm, "end": v(-32.89, -5) * mm});
            skPoint(sketch, "E31.0.midPoint", {"position": v(-34.33, -2.5) * mm});
            skLineSegment(sketch, "E32", {"start": v(-16.74, 4) * mm, "end": v(-26.54, 4) * mm});
            skLineSegment(sketch, "E33", {"start": v(-26.54, 4) * mm, "end": v(-26.54, -4) * mm});
            skLineSegment(sketch, "E34", {"start": v(-26.54, -4) * mm, "end": v(-16.74, -4) * mm});
            skLineSegment(sketch, "E35", {"start": v(-16.74, -4) * mm, "end": v(-11.84, -4) * mm});
            skLineSegment(sketch, "E36", {"start": v(-11.84, -4) * mm, "end": v(-9.38, -8.25) * mm});
            skLineSegment(sketch, "E37", {"start": v(-9.38, -8.25) * mm, "end": v(-11.84, -12.5) * mm});
            skLineSegment(sketch, "E38.1.0", {"start": v(-20.77, -25.98) * mm, "end": v(-17.89, -20.98) * mm});
            skLineSegment(sketch, "E38.1.1", {"start": v(-17.89, -30.98) * mm, "end": v(-20.77, -25.98) * mm});
            skLineSegment(sketch, "E38.1.2", {"start": v(-12.11, -30.98) * mm, "end": v(-17.89, -30.98) * mm});
            skLineSegment(sketch, "E38.1.3", {"start": v(-9.23, -25.98) * mm, "end": v(-12.11, -30.98) * mm});
            skCircle(sketch, "E38.1.4", {"center": v(-15, -25.98) * mm, "radius": 5 * mm, "construction": true});
            skLineSegment(sketch, "E38.1.5", {"start": v(-17.89, -20.98) * mm, "end": v(-12.11, -20.98) * mm});
            skLineSegment(sketch, "E38.1.6", {"start": v(-11.84, -12.5) * mm, "end": v(-16.73, -20.98) * mm});
            skLineSegment(sketch, "E38.1.7", {"start": v(-9.8, -24.98) * mm, "end": v(-4.9, -16.5) * mm});
            skLineSegment(sketch, "E38.1.8", {"start": v(-12.11, -20.98) * mm, "end": v(-9.23, -25.98) * mm});
            skLineSegment(sketch, "E38.1.9", {"start": v(-4.9, -16.5) * mm, "end": v(-2.45, -12.25) * mm});
            skLineSegment(sketch, "E38.1.10", {"start": v(-2.45, -12.25) * mm, "end": v(2.45, -12.25) * mm});
            skLineSegment(sketch, "E38.1.11", {"start": v(2.45, -12.25) * mm, "end": v(4.9, -16.5) * mm});
            skLineSegment(sketch, "E38.2.0", {"start": v(12.11, -30.98) * mm, "end": v(9.23, -25.98) * mm});
            skLineSegment(sketch, "E38.2.1", {"start": v(17.89, -30.98) * mm, "end": v(12.11, -30.98) * mm});
            skLineSegment(sketch, "E38.2.2", {"start": v(20.77, -25.98) * mm, "end": v(17.89, -30.98) * mm});
            skLineSegment(sketch, "E38.2.3", {"start": v(17.89, -20.98) * mm, "end": v(20.77, -25.98) * mm});
            skCircle(sketch, "E38.2.4", {"center": v(15, -25.98) * mm, "radius": 5 * mm, "construction": true});
            skLineSegment(sketch, "E38.2.5", {"start": v(9.23, -25.98) * mm, "end": v(12.11, -20.98) * mm});
            skLineSegment(sketch, "E38.2.6", {"start": v(4.9, -16.5) * mm, "end": v(9.8, -24.98) * mm});
            skLineSegment(sketch, "E38.2.7", {"start": v(16.73, -20.98) * mm, "end": v(11.84, -12.5) * mm});
            skLineSegment(sketch, "E38.2.8", {"start": v(12.11, -20.98) * mm, "end": v(17.89, -20.98) * mm});
            skLineSegment(sketch, "E38.2.9", {"start": v(11.84, -12.5) * mm, "end": v(9.38, -8.25) * mm});
            skLineSegment(sketch, "E38.2.10", {"start": v(9.38, -8.25) * mm, "end": v(11.84, -4) * mm});
            skLineSegment(sketch, "E38.2.11", {"start": v(11.84, -4) * mm, "end": v(16.74, -4) * mm});
            skLineSegment(sketch, "E38.3.0", {"start": v(32.89, -5) * mm, "end": v(27.11, -5) * mm});
            skLineSegment(sketch, "E38.3.1", {"start": v(35.77, 0) * mm, "end": v(32.89, -5) * mm});
            skLineSegment(sketch, "E38.3.2", {"start": v(32.89, 5) * mm, "end": v(35.77, 0) * mm});
            skLineSegment(sketch, "E38.3.3", {"start": v(27.11, 5) * mm, "end": v(32.89, 5) * mm});
            skCircle(sketch, "E38.3.4", {"center": v(30, 0) * mm, "radius": 5 * mm, "construction": true});
            skLineSegment(sketch, "E38.3.5", {"start": v(27.11, -5) * mm, "end": v(24.23, 0) * mm});
            skLineSegment(sketch, "E38.3.6", {"start": v(16.74, -4) * mm, "end": v(26.54, -4) * mm});
            skLineSegment(sketch, "E38.3.7", {"start": v(26.54, 4) * mm, "end": v(16.74, 4) * mm});
            skLineSegment(sketch, "E38.3.8", {"start": v(24.23, 0) * mm, "end": v(27.11, 5) * mm});
            skLineSegment(sketch, "E38.3.9", {"start": v(16.74, 4) * mm, "end": v(11.84, 4) * mm});
            skLineSegment(sketch, "E38.3.10", {"start": v(11.84, 4) * mm, "end": v(9.38, 8.25) * mm});
            skLineSegment(sketch, "E38.3.11", {"start": v(9.38, 8.25) * mm, "end": v(11.84, 12.5) * mm});
            skLineSegment(sketch, "E38.4.0", {"start": v(20.77, 25.98) * mm, "end": v(17.89, 20.98) * mm});
            skLineSegment(sketch, "E38.4.1", {"start": v(17.89, 30.98) * mm, "end": v(20.77, 25.98) * mm});
            skLineSegment(sketch, "E38.4.2", {"start": v(12.11, 30.98) * mm, "end": v(17.89, 30.98) * mm});
            skLineSegment(sketch, "E38.4.3", {"start": v(9.23, 25.98) * mm, "end": v(12.11, 30.98) * mm});
            skCircle(sketch, "E38.4.4", {"center": v(15, 25.98) * mm, "radius": 5 * mm, "construction": true});
            skLineSegment(sketch, "E38.4.5", {"start": v(17.89, 20.98) * mm, "end": v(12.11, 20.98) * mm});
            skLineSegment(sketch, "E38.4.6", {"start": v(11.84, 12.5) * mm, "end": v(16.73, 20.98) * mm});
            skLineSegment(sketch, "E38.4.7", {"start": v(9.8, 24.98) * mm, "end": v(4.9, 16.5) * mm});
            skLineSegment(sketch, "E38.4.8", {"start": v(12.11, 20.98) * mm, "end": v(9.23, 25.98) * mm});
            skLineSegment(sketch, "E38.4.9", {"start": v(4.9, 16.5) * mm, "end": v(2.45, 12.25) * mm});
            skLineSegment(sketch, "E38.4.10", {"start": v(2.45, 12.25) * mm, "end": v(-2.45, 12.25) * mm});
            skLineSegment(sketch, "E38.4.11", {"start": v(-2.45, 12.25) * mm, "end": v(-4.9, 16.5) * mm});
            skLineSegment(sketch, "E38.5.0", {"start": v(-12.11, 30.98) * mm, "end": v(-9.23, 25.98) * mm});
            skLineSegment(sketch, "E38.5.1", {"start": v(-17.89, 30.98) * mm, "end": v(-12.11, 30.98) * mm});
            skLineSegment(sketch, "E38.5.2", {"start": v(-20.77, 25.98) * mm, "end": v(-17.89, 30.98) * mm});
            skLineSegment(sketch, "E38.5.3", {"start": v(-17.89, 20.98) * mm, "end": v(-20.77, 25.98) * mm});
            skCircle(sketch, "E38.5.4", {"center": v(-15, 25.98) * mm, "radius": 5 * mm, "construction": true});
            skLineSegment(sketch, "E38.5.5", {"start": v(-9.23, 25.98) * mm, "end": v(-12.11, 20.98) * mm});
            skLineSegment(sketch, "E38.5.6", {"start": v(-4.9, 16.5) * mm, "end": v(-9.8, 24.98) * mm});
            skLineSegment(sketch, "E38.5.7", {"start": v(-16.73, 20.98) * mm, "end": v(-11.84, 12.5) * mm});
            skLineSegment(sketch, "E38.5.8", {"start": v(-12.11, 20.98) * mm, "end": v(-17.89, 20.98) * mm});
            skLineSegment(sketch, "E38.5.9", {"start": v(-11.84, 12.5) * mm, "end": v(-9.38, 8.25) * mm});
            skLineSegment(sketch, "E38.5.10", {"start": v(-9.38, 8.25) * mm, "end": v(-11.84, 4) * mm});
            skLineSegment(sketch, "E38.5.11", {"start": v(-11.84, 4) * mm, "end": v(-16.74, 4) * mm});
            skPoint(sketch, "E38.center", {"position": v(0, 0) * mm});
            skSolve(sketch);
        }
        {
            var Q0;
            {var subQ2=sQuery(id+"F6.wireOp",EDGE,"E31.2");Q0=makeQuery(id+"F6.imprint","IMPRINT",FACE,{"disambiguationData":[TD([[makeQuery(id+"F6.imprint","IMPRINT",EDGE,{"derivedFrom":subQ2}),1.0]])]});}
            var Q1;
            {var subQ1=sQuery(id+"F6.wireOp",EDGE,"E38.4.3");Q1=makeQuery(id+"F6.imprint","IMPRINT",FACE,{"disambiguationData":[TD([[makeQuery(id+"F6.imprint","IMPRINT",EDGE,{"derivedFrom":subQ1}),1.0]])]});}
            var Q2;
            {var subQ1=sQuery(id+"F6.wireOp",EDGE,"E38.3.3");Q2=makeQuery(id+"F6.imprint","IMPRINT",FACE,{"disambiguationData":[TD([[makeQuery(id+"F6.imprint","IMPRINT",EDGE,{"derivedFrom":subQ1}),1.0]])]});}
            var Q3;
            {var subQ1=sQuery(id+"F6.wireOp",EDGE,"E38.2.3");Q3=makeQuery(id+"F6.imprint","IMPRINT",FACE,{"disambiguationData":[TD([[makeQuery(id+"F6.imprint","IMPRINT",EDGE,{"derivedFrom":subQ1}),1.0]])]});}
            var Q4;
            {var subQ1=sQuery(id+"F6.wireOp",EDGE,"E38.1.3");Q4=makeQuery(id+"F6.imprint","IMPRINT",FACE,{"disambiguationData":[TD([[makeQuery(id+"F6.imprint","IMPRINT",EDGE,{"derivedFrom":subQ1}),1.0]])]});}
            var Q5;
            {var subQ4=sQuery(id+"F6.wireOp",EDGE,"E31.5");Q5=makeQuery(id+"F6.imprint","IMPRINT",FACE,{"disambiguationData":[TD([[makeQuery(id+"F6.imprint","IMPRINT",EDGE,{"derivedFrom":subQ4}),1.0]])]});}
            extrude(context, id + "F7", {"entities" : qUnion([Q0, Q1, Q2, Q3, Q4, Q5]), "operationType" : NewBodyOperationType.REMOVE, "oppositeDirection" : true, "depth" : 5 * mm, "offsetDistance" : 25 * mm});
        }
    });
